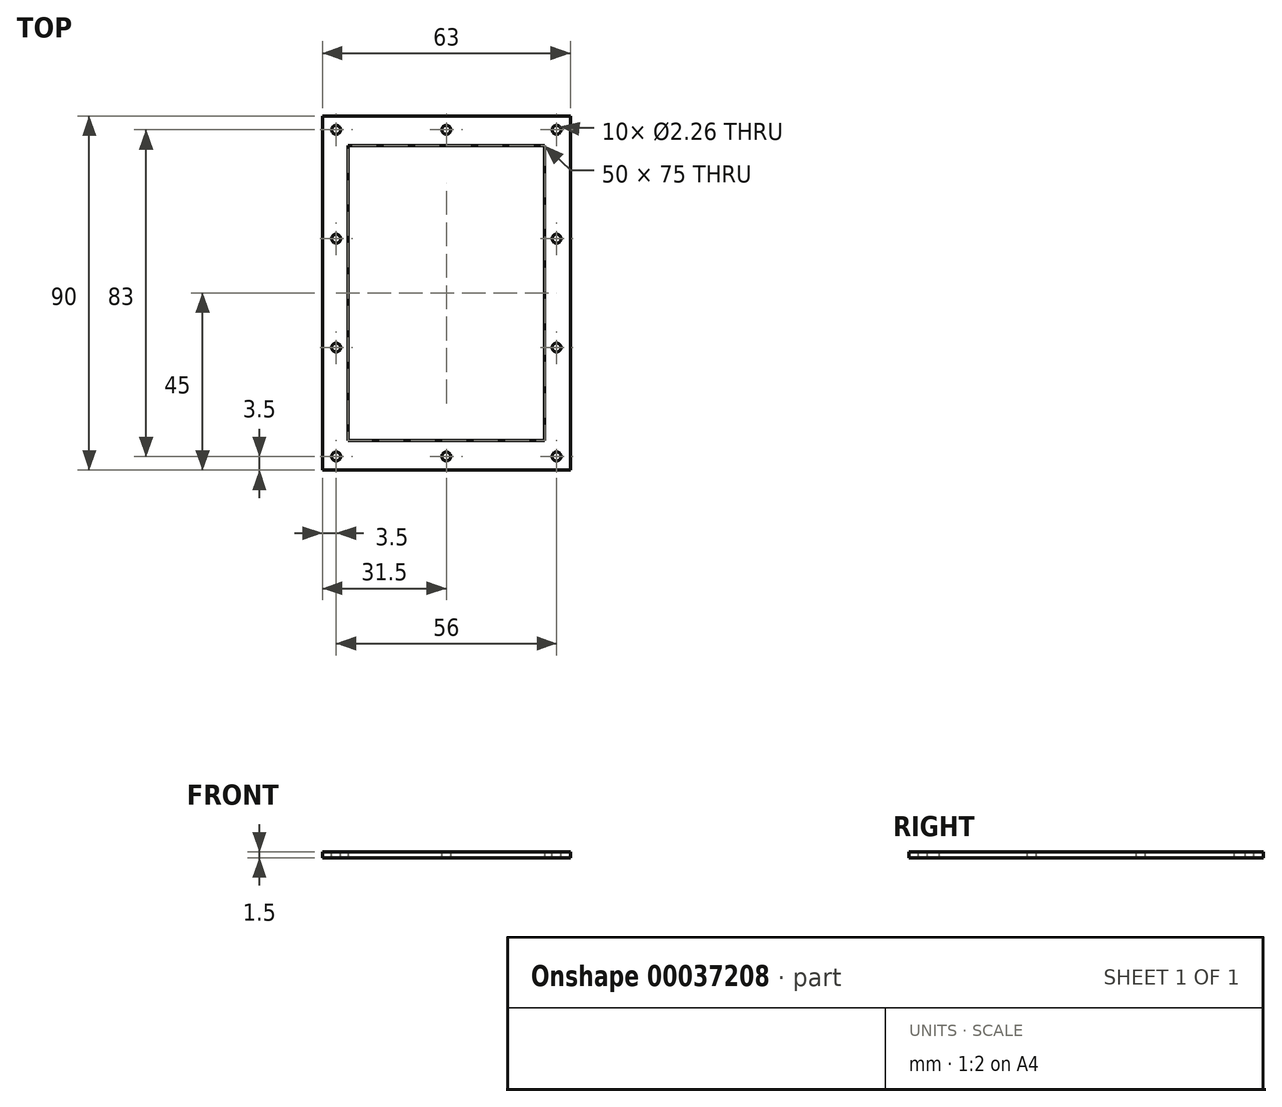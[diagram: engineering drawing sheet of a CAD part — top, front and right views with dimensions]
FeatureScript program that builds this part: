
annotation { "Feature Type Name" : "Feature", "Feature Type Description" : "" }
export const myFeature = defineFeature(function(context is Context, id is Id, definition is map)
    precondition{}
    {
        {
            var Q0;
            Q0=qCreatedBy(makeId("Top.planeOp"),FACE);
            var sketch = newSketch(context, id + "F0", { "sketchPlane" : qUnion([Q0])});
            skLineSegment(sketch, "E0.rect.bottom", {"start": v(25, 37.5) * mm, "end": v(-25, 37.5) * mm});
            skLineSegment(sketch, "E0.rect.top", {"start": v(25, -37.5) * mm, "end": v(-25, -37.5) * mm});
            skLineSegment(sketch, "E0.rect.left", {"start": v(25, 37.5) * mm, "end": v(25, -37.5) * mm});
            skLineSegment(sketch, "E0.rect.right", {"start": v(-25, 37.5) * mm, "end": v(-25, -37.5) * mm});
            skPoint(sketch, "E0.rect.middle", {"position": v(0, 0) * mm});
            skLineSegment(sketch, "E1.rect.bottom", {"start": v(31.5, 45) * mm, "end": v(-31.5, 45) * mm});
            skLineSegment(sketch, "E1.rect.top", {"start": v(31.5, -45) * mm, "end": v(-31.5, -45) * mm});
            skLineSegment(sketch, "E1.rect.left", {"start": v(31.5, 45) * mm, "end": v(31.5, -45) * mm});
            skLineSegment(sketch, "E1.rect.right", {"start": v(-31.5, 45) * mm, "end": v(-31.5, -45) * mm});
            skSolve(sketch);
        }
        {
            var Q0;
            Q0=makeQuery(id+"F0.imprint","IMPRINT",FACE,{"disambiguationData":[TD([[makeQuery(id+"F0.imprint","IMPRINT",EDGE,{"derivedFrom":sQuery(id+"F0.wireOp",EDGE,"E0.rect.bottom")}),-1.0]])]});
            extrude(context, id + "F1", {"entities" : qUnion([Q0]), "depth" : 1.5 * mm});
        }
        {
            var Q0;
            Q0=makeQuery(id+"F1.opExtrude","CAP_FACE",FACE,{"disambiguationData":[OSD([sQuery(id+"F0.wireOp",EDGE,"E0.rect.bottom"),sQuery(id+"F0.wireOp",EDGE,"E0.rect.top"),sQuery(id+"F0.wireOp",EDGE,"E0.rect.left"),sQuery(id+"F0.wireOp",EDGE,"E0.rect.right"),sQuery(id+"F0.wireOp",EDGE,"E1.rect.bottom"),sQuery(id+"F0.wireOp",EDGE,"E1.rect.top"),sQuery(id+"F0.wireOp",EDGE,"E1.rect.left"),sQuery(id+"F0.wireOp",EDGE,"E1.rect.right")])],"isStart":false});
            var sketch = newSketch(context, id + "F2", { "sketchPlane" : qUnion([Q0])});
            skLineSegment(sketch, "E2.rect.bottom", {"start": v(28, 41.5) * mm, "end": v(-28, 41.5) * mm, "construction": true});
            skLineSegment(sketch, "E2.rect.top", {"start": v(28, -41.5) * mm, "end": v(-28, -41.5) * mm, "construction": true});
            skLineSegment(sketch, "E2.rect.left", {"start": v(28, 41.5) * mm, "end": v(28, -41.5) * mm, "construction": true});
            skLineSegment(sketch, "E2.rect.right", {"start": v(-28, 41.5) * mm, "end": v(-28, -41.5) * mm, "construction": true});
            skPoint(sketch, "E2.rect.middle", {"position": v(0, 0) * mm});
            skPoint(sketch, "E3", {"position": v(0, 41.5) * mm});
            skPoint(sketch, "E4", {"position": v(28, 13.83) * mm});
            skPoint(sketch, "E5", {"position": v(28, -13.83) * mm});
            skPoint(sketch, "E6", {"position": v(0, -41.5) * mm});
            skPoint(sketch, "E7", {"position": v(-28, -13.83) * mm});
            skPoint(sketch, "E8", {"position": v(-28, 13.83) * mm});
            skCircle(sketch, "E9", {"center": v(0, 41.5) * mm, "radius": 1.13 * mm});
            skCircle(sketch, "E10", {"center": v(28, 41.5) * mm, "radius": 1.13 * mm});
            skCircle(sketch, "E11", {"center": v(28, -13.83) * mm, "radius": 1.13 * mm});
            skCircle(sketch, "E12", {"center": v(28, -41.5) * mm, "radius": 1.13 * mm});
            skCircle(sketch, "E13", {"center": v(0, -41.5) * mm, "radius": 1.13 * mm});
            skCircle(sketch, "E14", {"center": v(-28, -41.5) * mm, "radius": 1.13 * mm});
            skCircle(sketch, "E15", {"center": v(-28, -13.83) * mm, "radius": 1.13 * mm});
            skCircle(sketch, "E16", {"center": v(-28, 13.83) * mm, "radius": 1.13 * mm});
            skCircle(sketch, "E17", {"center": v(-28, 41.5) * mm, "radius": 1.13 * mm});
            skCircle(sketch, "E18", {"center": v(28, 13.83) * mm, "radius": 1.13 * mm});
            skSolve(sketch);
        }
        {
            var Q0;
            Q0 = qSketchRegion(id + "F2", true);
            extrude(context, id + "F3", {"entities" : qUnion([Q0]), "operationType" : NewBodyOperationType.REMOVE, "oppositeDirection" : true, "depth" : 25 * mm});
        }
    });
